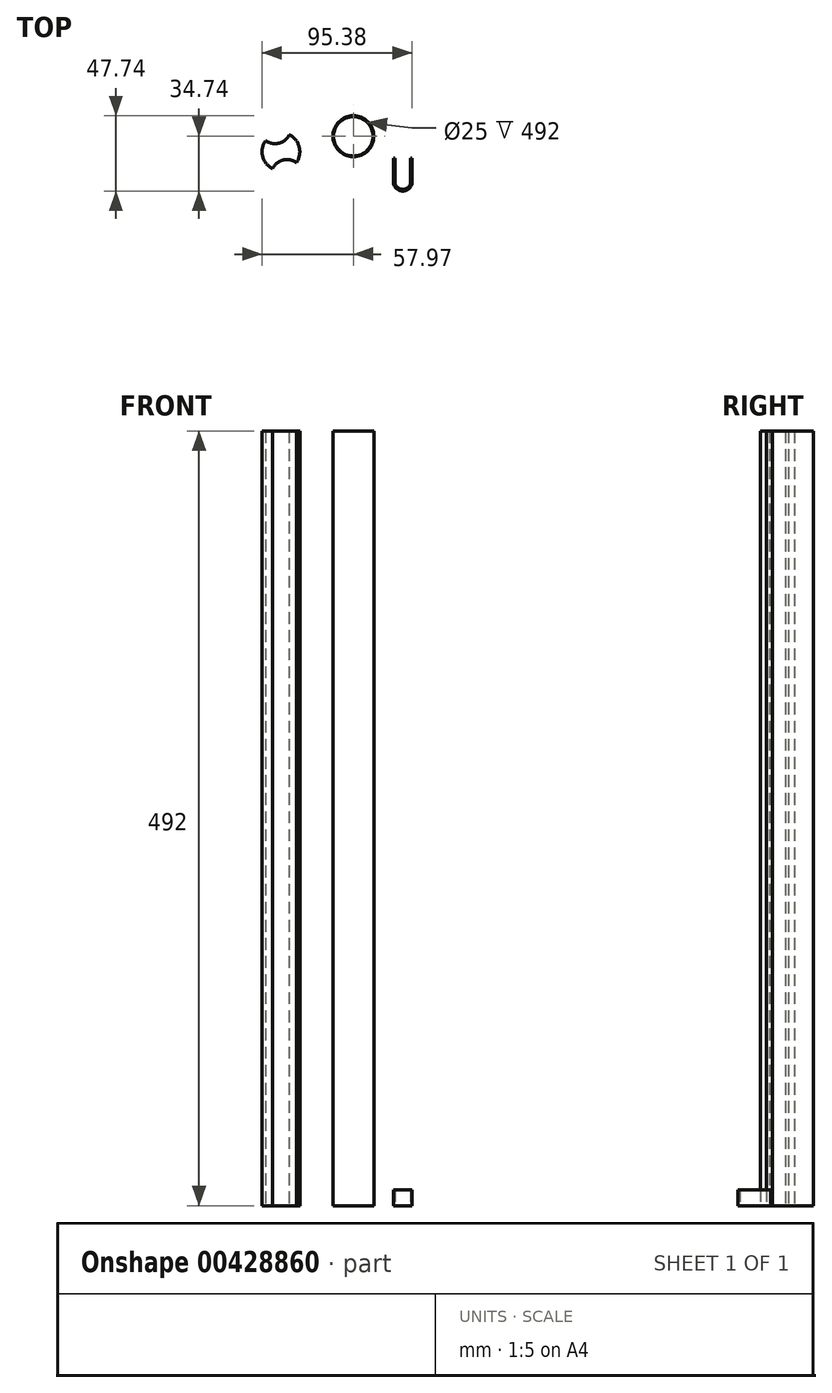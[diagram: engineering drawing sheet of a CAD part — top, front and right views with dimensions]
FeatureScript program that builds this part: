
annotation { "Feature Type Name" : "Feature", "Feature Type Description" : "" }
export const myFeature = defineFeature(function(context is Context, id is Id, definition is map)
    precondition{}
    {
        {
            var Q0;
            Q0=qCreatedBy(makeId("Top.planeOp"),FACE);
            var sketch = newSketch(context, id + "F0", { "sketchPlane" : qUnion([Q0])});
            skCircle(sketch, "E0", {"center": v(0, 0) * mm, "radius": 13 * mm});
            skCircle(sketch, "E1", {"center": v(0, 0) * mm, "radius": 12.5 * mm});
            skArc(sketch, "E2", {"start": v(-55.7, -2.72) * mm, "mid": v(-47.32, -4.39) * mm, "end": v(-40.7, 1.05) * mm});
            skArc(sketch, "E3", {"start": v(-36.23, -16.75) * mm, "mid": v(-44.63, -15.09) * mm, "end": v(-51.23, -20.52) * mm});
            skArc(sketch, "E4", {"start": v(-55.7, -2.72) * mm, "mid": v(-57.6, -12.66) * mm, "end": v(-51.23, -20.52) * mm});
            skArc(sketch, "E5", {"start": v(-36.23, -16.75) * mm, "mid": v(-34.33, -6.81) * mm, "end": v(-40.7, 1.05) * mm});
            skSolve(sketch);
        }
        {
            var Q0;
            Q0 = qSketchRegion(id + "F0", true);
            extrude(context, id + "F1", {"entities" : qUnion([Q0]), "depth" : 492 * mm});
        }
        {
            var Q0;
            Q0=qCreatedBy(makeId("Top.planeOp"),FACE);
            var sketch = newSketch(context, id + "F2", { "sketchPlane" : qUnion([Q0])});
            skLineSegment(sketch, "E6", {"start": v(26.41, -13.74) * mm, "end": v(26.41, -28.74) * mm});
            skLineSegment(sketch, "E7", {"start": v(36.41, -13.74) * mm, "end": v(36.41, -28.74) * mm});
            skArc(sketch, "E8", {"start": v(26.41, -28.74) * mm, "mid": v(31.41, -33.74) * mm, "end": v(36.41, -28.74) * mm});
            skLineSegment(sketch, "E9", {"start": v(25.41, -13.74) * mm, "end": v(25.41, -28.74) * mm});
            skLineSegment(sketch, "E10", {"start": v(37.41, -13.74) * mm, "end": v(37.41, -28.74) * mm});
            skArc(sketch, "E11", {"start": v(25.41, -28.74) * mm, "mid": v(31.41, -34.74) * mm, "end": v(37.41, -28.74) * mm});
            skLineSegment(sketch, "E12", {"start": v(25.41, -13.74) * mm, "end": v(26.41, -13.74) * mm});
            skLineSegment(sketch, "E13", {"start": v(36.41, -13.74) * mm, "end": v(37.41, -13.74) * mm});
            skSolve(sketch);
        }
        {
            var Q0;
            Q0 = qSketchRegion(id + "F2", true);
            extrude(context, id + "F3", {"entities" : qUnion([Q0]), "depth" : 10 * mm});
        }
    });
